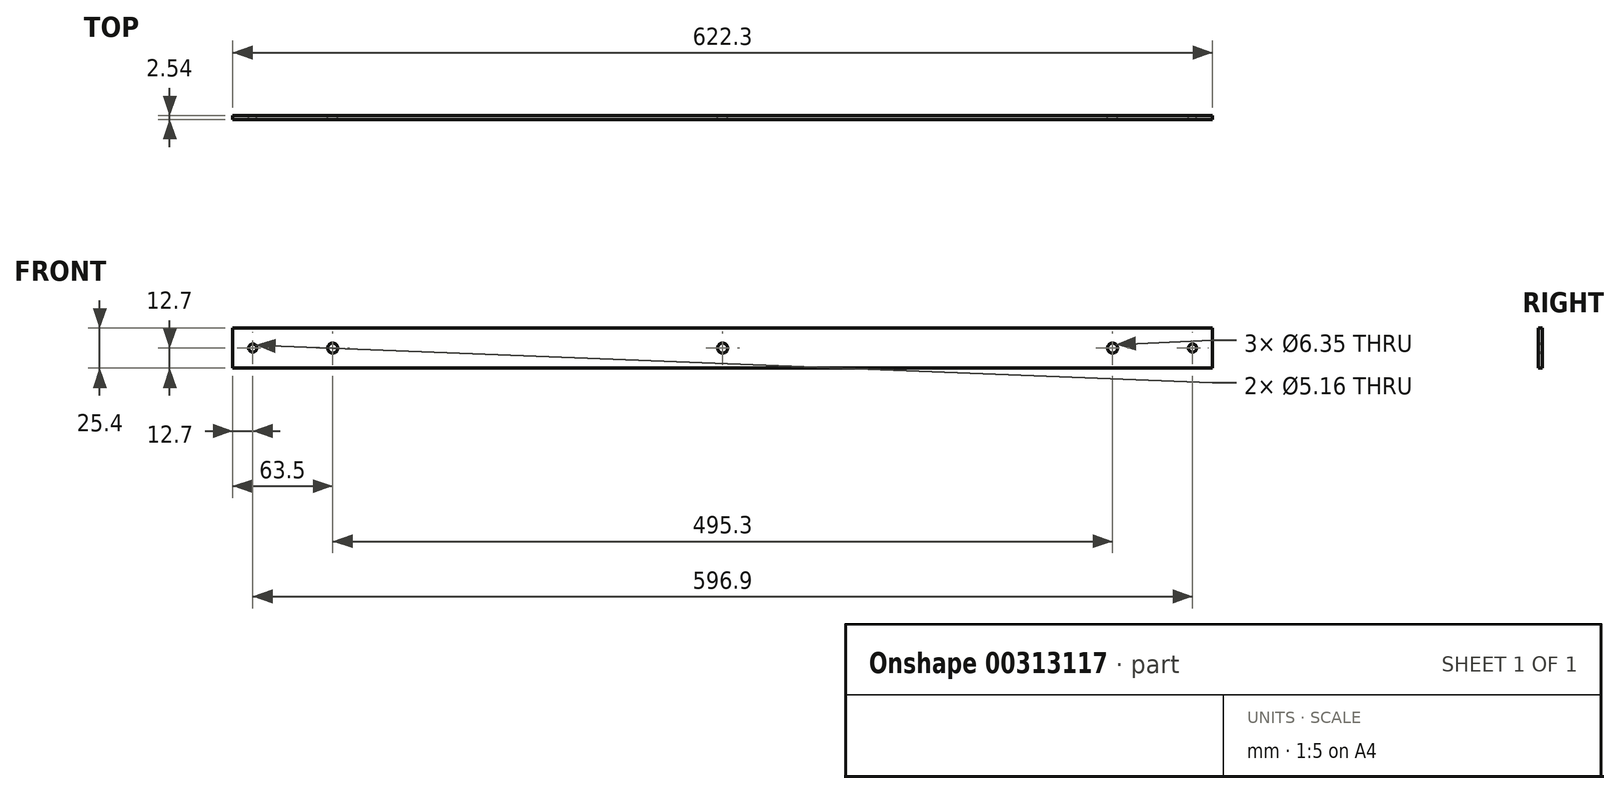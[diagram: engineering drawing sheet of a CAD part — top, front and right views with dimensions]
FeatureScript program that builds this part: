
annotation { "Feature Type Name" : "Feature", "Feature Type Description" : "" }
export const myFeature = defineFeature(function(context is Context, id is Id, definition is map)
    precondition{}
    {
        {
            var Q0;
            Q0=qCreatedBy(makeId("Front.planeOp"),FACE);
            var sketch = newSketch(context, id + "F0", { "sketchPlane" : qUnion([Q0])});
            skLineSegment(sketch, "E0.bottom", {"start": v(311.15, 0) * mm, "end": v(-311.15, 0) * mm});
            skLineSegment(sketch, "E0.top", {"start": v(311.15, -25.4) * mm, "end": v(-311.15, -25.4) * mm});
            skLineSegment(sketch, "E0.left", {"start": v(311.15, 0) * mm, "end": v(311.15, -25.4) * mm});
            skLineSegment(sketch, "E0.right", {"start": v(-311.15, 0) * mm, "end": v(-311.15, -25.4) * mm});
            skCircle(sketch, "E1", {"center": v(0, -12.7) * mm, "radius": 3.18 * mm});
            skPoint(sketch, "E1.centerSnap0", {"position": v(0, 0) * mm});
            skCircle(sketch, "E2", {"center": v(-247.65, -12.7) * mm, "radius": 3.18 * mm});
            skCircle(sketch, "E3", {"center": v(247.65, -12.7) * mm, "radius": 3.18 * mm});
            skCircle(sketch, "E4", {"center": v(-298.45, -12.7) * mm, "radius": 2.58 * mm});
            skCircle(sketch, "E5", {"center": v(298.45, -12.7) * mm, "radius": 2.58 * mm});
            skSolve(sketch);
        }
        {
            var Q0;
            Q0 = qSketchRegion(id + "F0", true);
            extrude(context, id + "F1", {"entities" : qUnion([Q0]), "depth" : 2.54 * mm});
        }
    });
